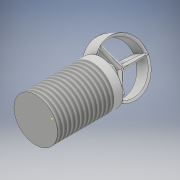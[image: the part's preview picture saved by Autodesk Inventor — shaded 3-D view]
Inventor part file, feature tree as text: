
AUTODESK INVENTOR PART (.ipt)
format: ipt  version: 2017 (Build 210142000, 142)  size: 260,096 bytes
history: native  units: mm
features: sketch x6, extrude x3, fillet x2, thread x1
ambient origin geometry x8: Origin, YZ Plane, XZ Plane, XY Plane, X Axis, Y Axis, Z Axis, Center Point
bodies: Solid1 (feature_tree)
feature tree (12):
  extrude  "Extrusion1"  Depth=10.0mm TaperAngle=0.0deg
  extrude  "Extrusion2"  Depth=0.5mm TaperAngle=0.0deg
  sketch  "3D Sketch1"
  extrude  "Extrusion3"  Depth=0.5mm
  fillet  "Fillet1"  Radius=0.5mm
  sketch  "Sketch4"
  sketch  "Sketch5"
  thread  "Thread1"  [1 undecoded]
  fillet  "Fillet2"  [1 undecoded]
  sketch  "Sketch1"  dims[d0=10.0mm d1=15.0mm d2=0.0mm]
  sketch  "Sketch2"  dims[d3=0.5mm d4=0.0mm d5=3.5mm d6=0.0mm]
  sketch  "Sketch3"  dims[d7=0.5mm d8=15.0mm d9=2.0mm d10=0.5mm]
note: 2 required parameter values undecoded (feature->parameter linkage not recoverable at this tier; creation-order binding heuristic only, values carry confidence <= 0.55)
